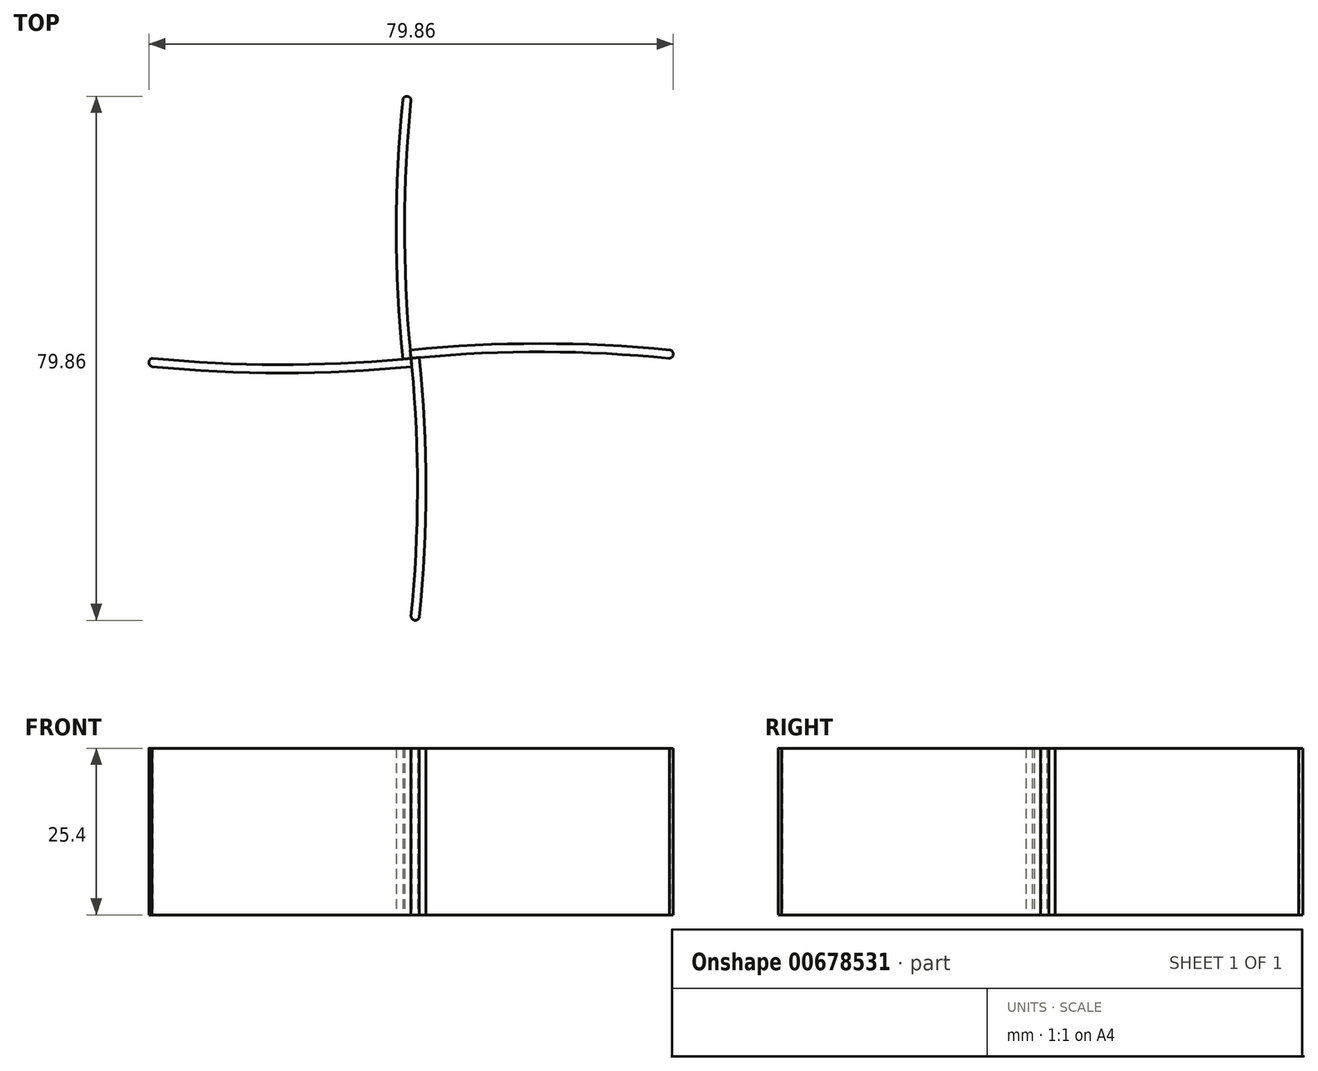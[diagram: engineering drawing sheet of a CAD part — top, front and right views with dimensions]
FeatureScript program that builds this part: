
annotation { "Feature Type Name" : "Feature", "Feature Type Description" : "" }
export const myFeature = defineFeature(function(context is Context, id is Id, definition is map)
    precondition{}
    {
        {
            var Q0;
            Q0=qCreatedBy(makeId("Top.planeOp"),FACE);
            var sketch = newSketch(context, id + "F0", { "sketchPlane" : qUnion([Q0])});
            skArc(sketch, "E0", {"start": v(39.32, 0) * mm, "mid": v(19.66, 0.98) * mm, "end": v(0, 0) * mm});
            skArc(sketch, "E1.0", {"start": v(39.45, 1.26) * mm, "mid": v(19.66, 2.25) * mm, "end": v(-0.13, 1.26) * mm});
            skArc(sketch, "E2", {"start": v(39.32, 0) * mm, "mid": v(39.93, 0.58) * mm, "end": v(39.45, 1.26) * mm});
            skLineSegment(sketch, "E3", {"start": v(-0.13, 1.26) * mm, "end": v(0, 0) * mm});
            skArc(sketch, "E4.1.0", {"start": v(0, 39.32) * mm, "mid": v(-0.98, 19.66) * mm, "end": v(0, 0) * mm});
            skArc(sketch, "E4.1.1", {"start": v(-1.26, 39.45) * mm, "mid": v(-2.25, 19.66) * mm, "end": v(-1.26, -0.13) * mm});
            skLineSegment(sketch, "E4.1.2", {"start": v(-1.26, -0.13) * mm, "end": v(0, 0) * mm});
            skArc(sketch, "E4.1.3", {"start": v(0, 39.32) * mm, "mid": v(-0.58, 39.93) * mm, "end": v(-1.26, 39.45) * mm});
            skArc(sketch, "E4.2.0", {"start": v(-39.32, 0) * mm, "mid": v(-19.66, -0.98) * mm, "end": v(0, 0) * mm});
            skArc(sketch, "E4.2.1", {"start": v(-39.45, -1.26) * mm, "mid": v(-19.66, -2.25) * mm, "end": v(0.13, -1.26) * mm});
            skLineSegment(sketch, "E4.2.2", {"start": v(0.13, -1.26) * mm, "end": v(0, 0) * mm});
            skArc(sketch, "E4.2.3", {"start": v(-39.32, 0) * mm, "mid": v(-39.93, -0.58) * mm, "end": v(-39.45, -1.26) * mm});
            skArc(sketch, "E4.3.0", {"start": v(0, -39.32) * mm, "mid": v(0.98, -19.66) * mm, "end": v(0, 0) * mm});
            skArc(sketch, "E4.3.1", {"start": v(1.26, -39.45) * mm, "mid": v(2.25, -19.66) * mm, "end": v(1.26, 0.13) * mm});
            skLineSegment(sketch, "E4.3.2", {"start": v(1.26, 0.13) * mm, "end": v(0, 0) * mm});
            skArc(sketch, "E4.3.3", {"start": v(0, -39.32) * mm, "mid": v(0.58, -39.93) * mm, "end": v(1.26, -39.45) * mm});
            skPoint(sketch, "E4.center", {"position": v(0, 0) * mm});
            skSolve(sketch);
        }
        {
            var Q0;
            {var subQ4=sQuery(id+"F0.wireOp",EDGE,"E3");Q0=makeQuery(id+"F0.imprint","IMPRINT",FACE,{"disambiguationData":[TD([[makeQuery(id+"F0.imprint","IMPRINT",EDGE,{"derivedFrom":subQ4}),-1.0]])]});}
            var Q1;
            {var subQ0=sQuery(id+"F0.wireOp",EDGE,"E2");Q1=makeQuery(id+"F0.imprint","IMPRINT",FACE,{"disambiguationData":[TD([[makeQuery(id+"F0.imprint","IMPRINT",EDGE,{"derivedFrom":subQ0}),1.0]])]});}
            var Q2;
            {var subQ4=sQuery(id+"F0.wireOp",EDGE,"E4.2.2");Q2=makeQuery(id+"F0.imprint","IMPRINT",FACE,{"disambiguationData":[TD([[makeQuery(id+"F0.imprint","IMPRINT",EDGE,{"derivedFrom":subQ4}),-1.0]])]});}
            var Q3;
            {var subQ4=sQuery(id+"F0.wireOp",EDGE,"E4.1.2");Q3=makeQuery(id+"F0.imprint","IMPRINT",FACE,{"disambiguationData":[TD([[makeQuery(id+"F0.imprint","IMPRINT",EDGE,{"derivedFrom":subQ4}),-1.0]])]});}
            extrude(context, id + "F1", {"entities" : qUnion([Q0, Q1, Q2, Q3]), "depth" : 25.4 * mm, "offsetDistance" : 25.4 * mm});
        }
    });
